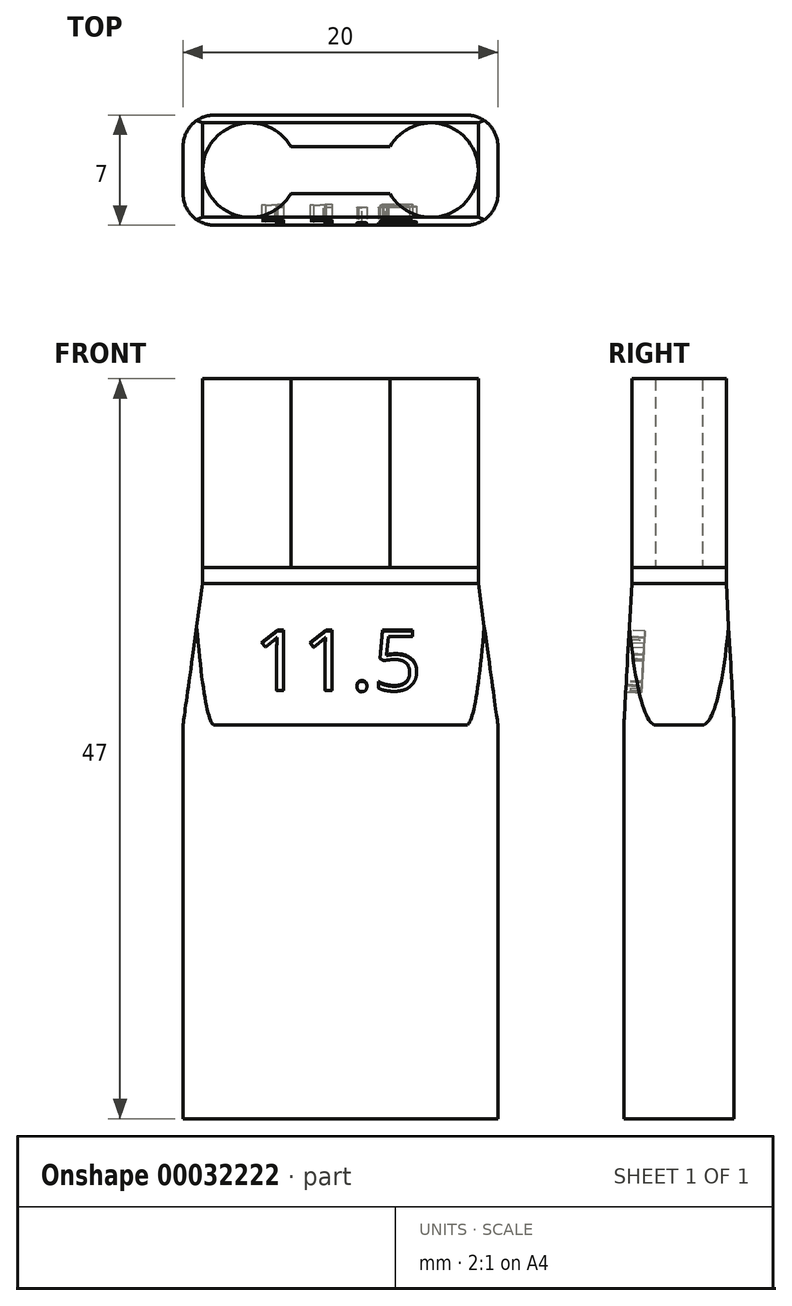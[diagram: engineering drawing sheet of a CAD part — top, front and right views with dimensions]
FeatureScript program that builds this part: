
annotation { "Feature Type Name" : "Feature", "Feature Type Description" : "" }
export const myFeature = defineFeature(function(context is Context, id is Id, definition is map)
    precondition{}
    {
        {
            var Q0;
            Q0=qCreatedBy(makeId("Top.planeOp"),FACE);
            var sketch = newSketch(context, id + "F0", { "sketchPlane" : qUnion([Q0])});
            skLineSegment(sketch, "E0", {"start": v(-5.75, 0) * mm, "end": v(5.75, 0) * mm, "construction": true});
            skCircle(sketch, "E1", {"center": v(-5.75, 0) * mm, "radius": 3 * mm});
            skCircle(sketch, "E2", {"center": v(5.75, 0) * mm, "radius": 3 * mm});
            skLineSegment(sketch, "E3.rect.bottom", {"start": v(3.15, 1.5) * mm, "end": v(-3.15, 1.5) * mm});
            skLineSegment(sketch, "E3.rect.top", {"start": v(3.15, -1.5) * mm, "end": v(-3.15, -1.5) * mm});
            skLineSegment(sketch, "E3.rect.left", {"start": v(3.15, 1.5) * mm, "end": v(3.15, -1.5) * mm});
            skLineSegment(sketch, "E3.rect.right", {"start": v(-3.15, 1.5) * mm, "end": v(-3.15, -1.5) * mm});
            skPoint(sketch, "E3.rect.middle", {"position": v(0, 0) * mm});
            skSolve(sketch);
        }
        {
            var Q0;
            Q0=qSketchRegion(id+"F0",true);
            extrude(context, id + "F1", {"entities" : qUnion([Q0]), "depth" : 12 * mm});
        }
        {
            var Q0;
            Q0=makeQuery(id+"F1.opExtrude","CAP_FACE",FACE,{"disambiguationData":[OSD([sQuery(id+"F0.wireOp",EDGE,"E1"),sQuery(id+"F0.wireOp",EDGE,"E2"),sQuery(id+"F0.wireOp",EDGE,"E3.rect.bottom"),sQuery(id+"F0.wireOp",EDGE,"E3.rect.top")])],"isStart":true});
            var sketch = newSketch(context, id + "F2", { "sketchPlane" : qUnion([Q0])});
            skLineSegment(sketch, "E4.rect.bottom", {"start": v(8.75, -3) * mm, "end": v(-8.75, -3) * mm});
            skLineSegment(sketch, "E4.rect.top", {"start": v(8.75, 3) * mm, "end": v(-8.75, 3) * mm});
            skLineSegment(sketch, "E4.rect.left", {"start": v(8.75, -3) * mm, "end": v(8.75, 3) * mm});
            skLineSegment(sketch, "E4.rect.right", {"start": v(-8.75, -3) * mm, "end": v(-8.75, 3) * mm});
            skPoint(sketch, "E4.rect.middle", {"position": v(0, 0) * mm});
            skPoint(sketch, "E4.rect.cornerSnap0", {"position": v(8.75, 0) * mm});
            skSolve(sketch);
        }
        {
            var Q0;
            {var subQ10=makeQuery(id+"F1.opExtrude","CAP_EDGE",EDGE,{"disambiguationData":[OSD([sQuery(id+"F0.wireOp",EDGE,"E3.rect.bottom")])],"isStart":true});Q0=makeQuery(id+"F2.imprint","IMPRINT",FACE,{"disambiguationData":[TD([[makeQuery(id+"F2.imprint","IMPRINT",EDGE,{"derivedFrom":subQ10}),-1.0]])]});}
            cPlane(context, id + "F3", {"entities" : qUnion([Q0]), "cplaneType" : CPlaneType.OFFSET, "offset" : 10 * mm, "width" : 150 * mm, "height" : 150 * mm});
        }
        {
            var Q0;
            Q0=qCreatedBy(id+"F3.planeOp",FACE);
            var sketch = newSketch(context, id + "F4", { "sketchPlane" : qUnion([Q0])});
            skLineSegment(sketch, "E5.rect.bottom", {"start": v(-10, 3.5) * mm, "end": v(10, 3.5) * mm});
            skLineSegment(sketch, "E5.rect.top", {"start": v(-10, -3.5) * mm, "end": v(10, -3.5) * mm});
            skLineSegment(sketch, "E5.rect.left", {"start": v(-10, 3.5) * mm, "end": v(-10, -3.5) * mm});
            skLineSegment(sketch, "E5.rect.right", {"start": v(10, 3.5) * mm, "end": v(10, -3.5) * mm});
            skPoint(sketch, "E5.rect.middle", {"position": v(0, 0) * mm});
            skSolve(sketch);
        }
        {
            var Q0;
            Q0=qSketchRegion(id+"F4",true);
            extrude(context, id + "F5", {"entities" : qUnion([Q0]), "depth" : 25 * mm});
        }
        {
            var Q0;
            Q0=qSketchRegion(id+"F2",true);
            extrude(context, id + "F6", {"entities" : qUnion([Q0]), "operationType" : NewBodyOperationType.ADD, "depth" : 1 * mm});
        }
        {
            var Q0;
            Q0=makeQuery(id+"F6.opExtrude","CAP_FACE",FACE,{"disambiguationData":[OSD([sQuery(id+"F2.wireOp",EDGE,"E4.rect.bottom"),sQuery(id+"F2.wireOp",EDGE,"E4.rect.top"),sQuery(id+"F2.wireOp",EDGE,"E4.rect.left"),sQuery(id+"F2.wireOp",EDGE,"E4.rect.right")])],"isStart":false});
            var Q1;
            Q1=makeQuery(id+"F5.opExtrude","CAP_FACE",FACE,{"disambiguationData":[OSD([sQuery(id+"F4.wireOp",EDGE,"E5.rect.bottom"),sQuery(id+"F4.wireOp",EDGE,"E5.rect.top"),sQuery(id+"F4.wireOp",EDGE,"E5.rect.left"),sQuery(id+"F4.wireOp",EDGE,"E5.rect.right")])],"isStart":true});
            loft(context, id + "F7", {"operationType" : NewBodyOperationType.ADD, "sheetProfilesArray" : [{ "sheetProfileEntities" : qUnion([Q0]) }, { "sheetProfileEntities" : qUnion([Q1]) }]});
        }
        {
            var Q0;
            Q0=makeQuery(id+"F7.opLoft","SWEPT_FACE",FACE,{"disambiguationData":[OSD([sQuery(id+"F2.wireOp",EDGE,"E4.rect.top"),sQuery(id+"F2.wireOp",EDGE,"E4.rect.left"),sQuery(id+"F2.wireOp",EDGE,"E4.rect.right"),sQuery(id+"F4.wireOp",EDGE,"E5.rect.bottom"),sQuery(id+"F4.wireOp",EDGE,"E5.rect.left"),sQuery(id+"F4.wireOp",EDGE,"E5.rect.right")])]});
            var sketch = newSketch(context, id + "F8", { "sketchPlane" : qUnion([Q0])});
            skText(sketch, "E6", { "text": "11.5", "fontName": "OpenSans-Regular.ttf"});
            const initialGuessF8  = {"E6": [-0.0055, -0.00798, 1, 0, 0.00387]};
            skSetInitialGuess(sketch, initialGuessF8);
            skSolve(sketch);
        }
        {
            var Q0;
            Q0=qSketchRegion(id+"F8",true);
            extrude(context, id + "F9", {"entities" : qUnion([Q0]), "operationType" : NewBodyOperationType.REMOVE, "oppositeDirection" : true, "depth" : 1 * mm});
        }
        {
            var Q0;
            Q0=makeQuery(id+"F5.opExtrude","SWEPT_EDGE",EDGE,{"disambiguationData":[OSD([sQuery(id+"F4.wireOp",EDGE,"E5.rect.bottom"),sQuery(id+"F4.wireOp",EDGE,"E5.rect.left")])]});
            var Q1;
            Q1=makeQuery(id+"F5.opExtrude","SWEPT_EDGE",EDGE,{"disambiguationData":[OSD([sQuery(id+"F4.wireOp",EDGE,"E5.rect.top"),sQuery(id+"F4.wireOp",EDGE,"E5.rect.left")])]});
            var Q2;
            Q2=makeQuery(id+"F5.opExtrude","SWEPT_EDGE",EDGE,{"disambiguationData":[OSD([sQuery(id+"F4.wireOp",EDGE,"E5.rect.top"),sQuery(id+"F4.wireOp",EDGE,"E5.rect.right")])]});
            var Q3;
            Q3=makeQuery(id+"F5.opExtrude","SWEPT_EDGE",EDGE,{"disambiguationData":[OSD([sQuery(id+"F4.wireOp",EDGE,"E5.rect.bottom"),sQuery(id+"F4.wireOp",EDGE,"E5.rect.right")])]});
            fillet(context, id + "F10", {"entities" : qUnion([Q0, Q1, Q2, Q3]), "radius" : 2 * mm, "tangentPropagation" : true, "allowEdgeOverflow" : false});
        }
    });
